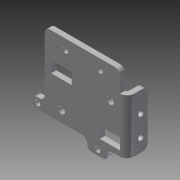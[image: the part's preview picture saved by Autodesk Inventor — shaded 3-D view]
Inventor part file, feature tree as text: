
AUTODESK INVENTOR PART (.ipt)
format: ipt  version: 2013 (Build 170138000, 138)  size: 269,824 bytes
history: native  units: in
note: dims shown in document units (in); Inventor stores cm internally (conversion verified against a paired STEP export)
features: sheet_metal_op x6, other x5, sketch x4, chamfer x1
ambient origin geometry x8: Origin, YZ Plane, XZ Plane, XY Plane, X Axis, Y Axis, Z Axis, Center Point
feature tree (16):
  sheet_metal_op  "Face2"
  sheet_metal_op  "Flange1"
  sheet_metal_op  "Face3"
  chamfer  "Corner Round1"
  sketch  "Sketch1"  dims[d0=0.5625in]
  other  "Plate2"
  sketch  "Sketch2"  dims[d3=0.5in]
  other  "Plate3"
  sheet_metal_op  "Bend1"
  sheet_metal_op  "Corner1"
  sketch  "Sketch3"  dims[d5=0.266in]
  sketch  "Sketch4"  dims[d6=0.5in d9=0.25in d10=0.25in d19=0.5in d20=0.266in d21=0.25in d22=0.125in d23=0.5in d24=0.25in d25=1.0in d26=90.0deg d27=0.0965in d28=1.0in d29=0.25in d30=0.25in d31=1.0in d32=1.0in d33=0.266in d34=0.266in d35=0.25in d36=0.0in d39=1.0in d40=1.0in d41=1.0in d42=0.266in d43=0.266in d44=0.25in d45=0.25in d46=0.125in d47=0.5in d48=0.25in d49=0.35in d50=0.25in d1=0.25in d2=0.125in d4=0.0in]
  other  "Plate4"
  sheet_metal_op  "Bend2"
  other  "Cut1"
  other  "Definition1"
